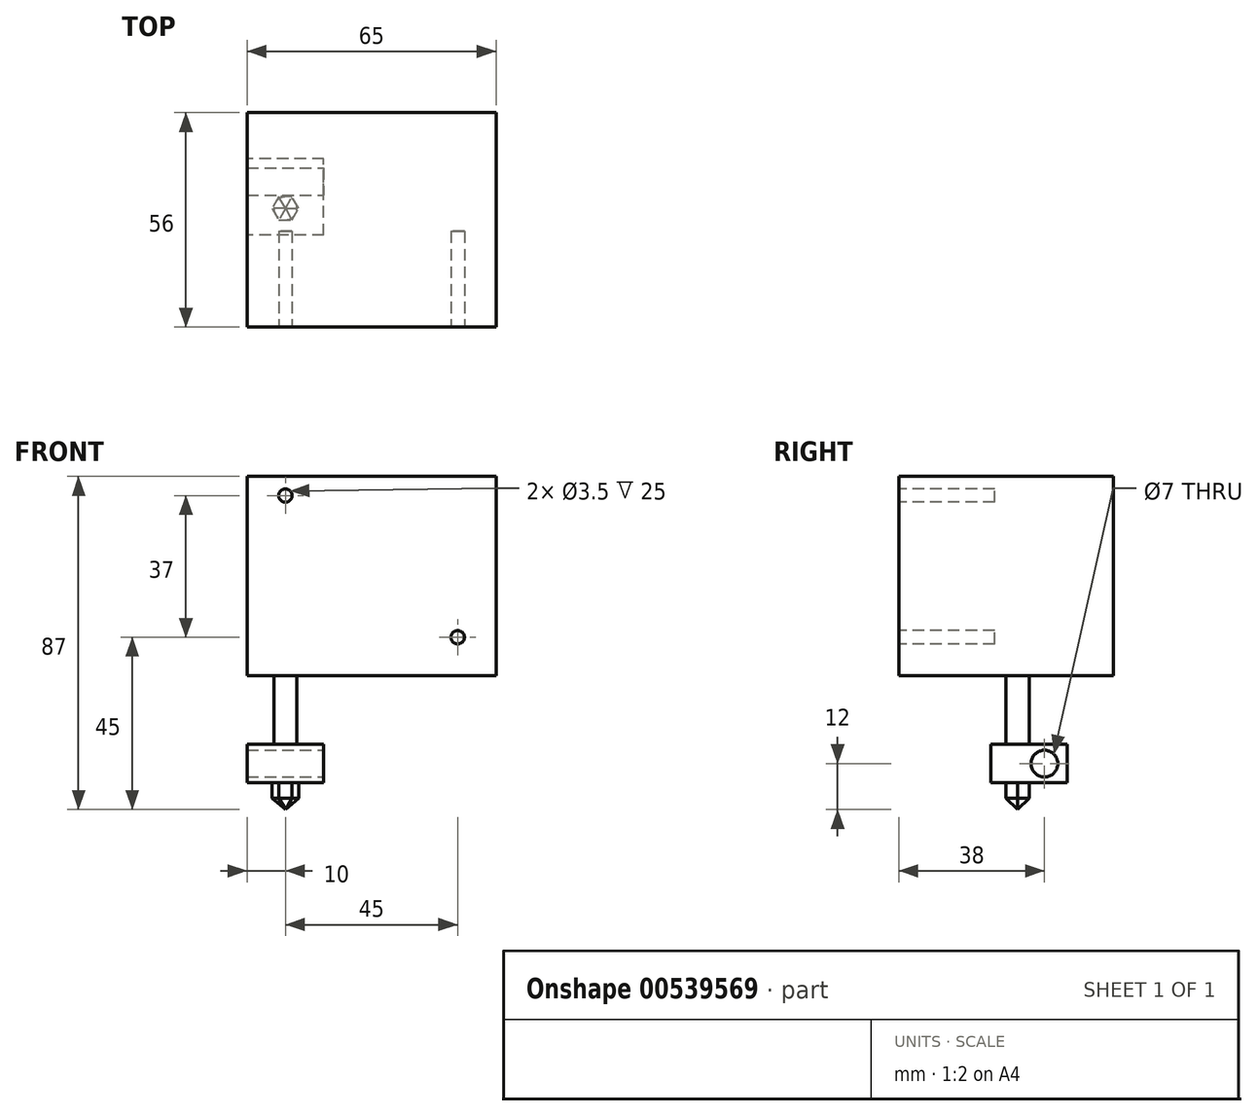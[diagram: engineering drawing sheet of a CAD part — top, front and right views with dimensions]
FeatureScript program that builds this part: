
annotation { "Feature Type Name" : "Feature", "Feature Type Description" : "" }
export const myFeature = defineFeature(function(context is Context, id is Id, definition is map)
    precondition{}
    {
        {
            var Q0;
            Q0=qCreatedBy(makeId("Top.planeOp"),FACE);
            var sketch = newSketch(context, id + "F0", { "sketchPlane" : qUnion([Q0])});
            skLineSegment(sketch, "E0.bottom", {"start": v(10, -10) * mm, "end": v(-10, -10) * mm});
            skLineSegment(sketch, "E0.top", {"start": v(10, 10) * mm, "end": v(-10, 10) * mm});
            skLineSegment(sketch, "E0.left", {"start": v(10, -10) * mm, "end": v(10, 10) * mm});
            skLineSegment(sketch, "E0.right", {"start": v(-10, -10) * mm, "end": v(-10, 10) * mm});
            skPoint(sketch, "E0.middle", {"position": v(0, 0) * mm});
            skSolve(sketch);
        }
        {
            var Q0;
            Q0=qSketchRegion(id+"F0",true);
            extrude(context, id + "F1", {"entities" : qUnion([Q0]), "depth" : 10 * mm, "offsetDistance" : 25 * mm});
        }
        {
            var Q0;
            Q0=makeQuery(id+"F1.opExtrude","SWEPT_FACE",FACE,{"disambiguationData":[OSD([sQuery(id+"F0.wireOp",EDGE,"E0.left")])]});
            var sketch = newSketch(context, id + "F2", { "sketchPlane" : qUnion([Q0])});
            skCircle(sketch, "E1", {"center": v(4, 5) * mm, "radius": 3.5 * mm});
            skPoint(sketch, "E1.centerSnap0", {"position": v(-10, 5) * mm});
            skSolve(sketch);
        }
        {
            var Q0;
            Q0=qSketchRegion(id+"F2",true);
            extrude(context, id + "F3", {"entities" : qUnion([Q0]), "operationType" : NewBodyOperationType.REMOVE, "endBound" : BoundingType.THROUGH_ALL, "oppositeDirection" : true, "depth" : 25 * mm, "offsetDistance" : 25 * mm});
        }
        {
            var Q0;
            Q0=makeQuery(id+"F1.opExtrude","CAP_FACE",FACE,{"disambiguationData":[OSD([sQuery(id+"F0.wireOp",EDGE,"E0.bottom"),sQuery(id+"F0.wireOp",EDGE,"E0.top"),sQuery(id+"F0.wireOp",EDGE,"E0.left"),sQuery(id+"F0.wireOp",EDGE,"E0.right")])],"isStart":false});
            var sketch = newSketch(context, id + "F4", { "sketchPlane" : qUnion([Q0])});
            skCircle(sketch, "E2", {"center": v(0, -3) * mm, "radius": 3 * mm});
            skSolve(sketch);
        }
        {
            var Q0;
            Q0=makeQuery(id+"F4.imprint","IMPRINT",FACE,{"disambiguationData":[TD([[makeQuery(id+"F4.imprint","IMPRINT",EDGE,{"derivedFrom":sQuery(id+"F4.wireOp",EDGE,"E2")}),1.0]])]});
            extrude(context, id + "F5", {"entities" : qUnion([Q0]), "operationType" : NewBodyOperationType.ADD, "depth" : 35 * mm, "offsetDistance" : 25 * mm});
        }
        {
            var Q0;
            Q0=makeQuery(id+"F1.opExtrude","CAP_FACE",FACE,{"disambiguationData":[OSD([sQuery(id+"F0.wireOp",EDGE,"E0.bottom"),sQuery(id+"F0.wireOp",EDGE,"E0.top"),sQuery(id+"F0.wireOp",EDGE,"E0.left"),sQuery(id+"F0.wireOp",EDGE,"E0.right")])],"isStart":true});
            var sketch = newSketch(context, id + "F6", { "sketchPlane" : qUnion([Q0])});
            skPoint(sketch, "E3.0", {"position": v(0, 3) * mm});
            skCircle(sketch, "E4.cCircle", {"center": v(0, 3) * mm, "radius": 3 * mm, "construction": true});
            skLineSegment(sketch, "E4.0", {"start": v(-1.73, 0) * mm, "end": v(-3.46, 3) * mm});
            skLineSegment(sketch, "E4.1", {"start": v(-3.46, 3) * mm, "end": v(-1.73, 6) * mm});
            skLineSegment(sketch, "E4.2", {"start": v(-1.73, 6) * mm, "end": v(1.73, 6) * mm});
            skLineSegment(sketch, "E4.3", {"start": v(1.73, 6) * mm, "end": v(3.46, 3) * mm});
            skLineSegment(sketch, "E4.4", {"start": v(3.46, 3) * mm, "end": v(1.73, 0) * mm});
            skLineSegment(sketch, "E4.5", {"start": v(1.73, 0) * mm, "end": v(-1.73, 0) * mm});
            skPoint(sketch, "E4.0.midPoint", {"position": v(-2.6, 1.5) * mm});
            skSolve(sketch);
        }
        {
            var Q0;
            Q0=qSketchRegion(id+"F6",true);
            extrude(context, id + "F7", {"entities" : qUnion([Q0]), "operationType" : NewBodyOperationType.ADD, "depth" : 4 * mm, "offsetDistance" : 25 * mm});
        }
        {
            var Q0;
            Q0=makeQuery(id+"F7.opExtrude","CAP_FACE",FACE,{"disambiguationData":[OSD([sQuery(id+"F6.wireOp",EDGE,"E4.0"),sQuery(id+"F6.wireOp",EDGE,"E4.1"),sQuery(id+"F6.wireOp",EDGE,"E4.2"),sQuery(id+"F6.wireOp",EDGE,"E4.3"),sQuery(id+"F6.wireOp",EDGE,"E4.4"),sQuery(id+"F6.wireOp",EDGE,"E4.5")])],"isStart":false});
            extrude(context, id + "F8", {"entities" : qUnion([Q0]), "operationType" : NewBodyOperationType.ADD, "depth" : 4 * mm, "offsetDistance" : 25 * mm, "hasDraft" : true, "draftAngle" : 45 * degree, "draftPullDirection" : true});
        }
        {
            var Q0;
            Q0=qCreatedBy(makeId("Right.planeOp"),FACE);
            var sketch = newSketch(context, id + "F9", { "sketchPlane" : qUnion([Q0])});
            skLineSegment(sketch, "E5.0", {"start": v(-3, -7) * mm, "end": v(-6, -4) * mm});
            skLineSegment(sketch, "E6.0", {"start": v(-3, -7) * mm, "end": v(0, -4) * mm});
            skLineSegment(sketch, "E7", {"start": v(-19.3, 5.59) * mm, "end": v(-32.72, 19.02) * mm});
            skPoint(sketch, "E7.startSnap0", {"position": v(-4.5, -5.5) * mm});
            skLineSegment(sketch, "E8", {"start": v(-32.72, 19.02) * mm, "end": v(-53.4, 19.02) * mm});
            skLineSegment(sketch, "E9", {"start": v(-53.4, 19.02) * mm, "end": v(-53.4, 7.42) * mm});
            skLineSegment(sketch, "E10", {"start": v(-53.4, 7.42) * mm, "end": v(-32.72, 7.42) * mm});
            skLineSegment(sketch, "E11", {"start": v(-32.72, 7.42) * mm, "end": v(-25.3, 0) * mm});
            skLineSegment(sketch, "E12", {"start": v(-25.3, 0) * mm, "end": v(-24.17, 1.13) * mm});
            skLineSegment(sketch, "E13", {"start": v(-24.17, 1.13) * mm, "end": v(-32.06, 9.02) * mm});
            skLineSegment(sketch, "E14", {"start": v(-32.06, 9.02) * mm, "end": v(-51.8, 9.02) * mm});
            skLineSegment(sketch, "E15", {"start": v(-51.8, 9.02) * mm, "end": v(-51.8, 17.42) * mm});
            skLineSegment(sketch, "E16", {"start": v(-51.8, 17.42) * mm, "end": v(-33.38, 17.42) * mm});
            skLineSegment(sketch, "E17", {"start": v(-33.38, 17.42) * mm, "end": v(-20.42, 4.46) * mm});
            skLineSegment(sketch, "E18", {"start": v(-20.42, 4.46) * mm, "end": v(-19.3, 5.59) * mm});
            skLineSegment(sketch, "E19", {"start": v(-3, -7) * mm, "end": v(-3, 50.23) * mm, "construction": true});
            skSolve(sketch);
        }
        {
            var Q0;
            Q0=qCreatedBy(makeId("Top.planeOp"),FACE);
            cPlane(context, id + "F10", {"entities" : qUnion([Q0]), "cplaneType" : CPlaneType.OFFSET, "offset" : 28 * mm, "width" : 150 * mm, "height" : 150 * mm});
        }
        {
            var Q0;
            Q0=qCreatedBy(id+"F10.planeOp",FACE);
            var sketch = newSketch(context, id + "F11", { "sketchPlane" : qUnion([Q0])});
            skLineSegment(sketch, "E20.bottom", {"start": v(-10, 22) * mm, "end": v(55, 22) * mm});
            skLineSegment(sketch, "E20.top", {"start": v(-10, -34) * mm, "end": v(55, -34) * mm});
            skLineSegment(sketch, "E20.left", {"start": v(-10, 22) * mm, "end": v(-10, -34) * mm});
            skLineSegment(sketch, "E20.right", {"start": v(55, 22) * mm, "end": v(55, -34) * mm});
            skPoint(sketch, "E21.0", {"position": v(0, -3) * mm});
            skSolve(sketch);
        }
        {
            var Q0;
            Q0=qSketchRegion(id+"F11",true);
            extrude(context, id + "F12", {"entities" : qUnion([Q0]), "operationType" : NewBodyOperationType.ADD, "depth" : 52 * mm, "offsetDistance" : 25 * mm});
        }
        {
            var Q0;
            Q0=makeQuery(id+"F12.opExtrude","SWEPT_FACE",FACE,{"disambiguationData":[OSD([sQuery(id+"F11.wireOp",EDGE,"E20.top")])]});
            var sketch = newSketch(context, id + "F13", { "sketchPlane" : qUnion([Q0])});
            skCircle(sketch, "E22", {"center": v(0, 75) * mm, "radius": 1.75 * mm});
            skCircle(sketch, "E23", {"center": v(45, 38) * mm, "radius": 1.75 * mm});
            skSolve(sketch);
        }
        {
            var Q0;
            Q0=qSketchRegion(id+"F13",true);
            extrude(context, id + "F14", {"entities" : qUnion([Q0]), "operationType" : NewBodyOperationType.REMOVE, "oppositeDirection" : true, "depth" : 25 * mm, "offsetDistance" : 25 * mm});
        }
    });
